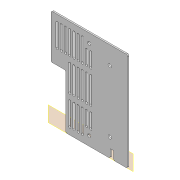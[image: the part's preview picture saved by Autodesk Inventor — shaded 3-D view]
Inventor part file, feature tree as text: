
AUTODESK INVENTOR PART (.ipt)
format: ipt  version: 2020 (Build 240168000, 168)  size: 770,048 bytes
history: native  units: mm
features: other x9, extrude x8, sketch x8, fillet x3, mirror x1
ambient origin geometry x8: Origin, YZ Plane, XZ Plane, XY Plane, X Axis, Y Axis, Z Axis, Center Point
bodies: Body1 (feature_tree)
feature tree (29):
  other  "Sólido1"
  other  "Plano de trabalho1"
  extrude  "Extrusão1"  Depth=0.5mm
  fillet  "Arredondamento2"  Radius=1.0mm
  extrude  "Extrusão5"  Depth=0.5mm
  mirror  "Espelhamento1"
  extrude  "Extrusão6"  Depth=4.5mm
  sketch  "Esboço7"  dims[d7=0.5mm d8=4.5mm]
  extrude  "Extrusão7"  Depth=4.5mm
  extrude  "Extrusão8"  Depth=10.0mm
  sketch  "Esboço9"  dims[d11=18.0mm d12=23.0mm]
  extrude  "Extrusão9"  Depth=18.0mm
  extrude  "Extrusão10"  Depth=31.0mm
  fillet  "Arredondamento3"  Radius=32.0mm
  fillet  "Arredondamento4"  Radius=32.0mm
  extrude  "Extrusão11"  Depth=2.0mm
  sketch  "Esboço1"  dims[d0=0.5mm d1=0.5mm d2=1.0mm]
  other  "Referência1"
  other  "Referência2"
  sketch  "Esboço5"  dims[d3=1.0mm d4=0.5mm]
  sketch  "Esboço6"  dims[d5=0.5mm d6=4.5mm]
  sketch  "Esboço8"  dims[d9=10.0mm d10=10.0mm]
  other  "Contorno projetado3"
  sketch  "Esboço10"  dims[d13=23.0mm d14=31.0mm d15=32.0mm d16=32.0mm]
  other  "Contorno projetado4"
  sketch  "Esboço11"  dims[d17=31.0mm d18=26.0mm d19=3.2mm d20=3.2mm d21=70.0mm d23=6.0mm d24=10.0mm d26=10.0mm d28=2.0mm d29=0.0mm d30=3.2mm d31=6.0mm d32=30.0mm d34=6.0mm d35=10.0mm d37=10.0mm d39=3.2mm d40=6.0mm d41=50.0mm d43=6.0mm d44=10.0mm d46=10.0mm d48=20.0mm d50=6.0mm d51=10.0mm d53=10.0mm d65=2.0mm d66=70.0mm d67=2.2mm d68=0.0mm d69=32.0mm d70=26.0mm d71=19.446305mm d72=32.276848mm d73=3.2mm d74=110.0mm d76=6.0mm d77=10.0mm d79=10.0mm d81=2.2mm d82=0.0mm d83=77.0mm d84=21.0mm d85=2.0mm d86=0.0mm d87=2.0mm d88=0.0mm d90=5.0mm d91=19.8mm d92=12.0mm d93=8.0mm d94=2.0mm d95=0.0mm d96=2.0mm d97=0.0mm d98=2.0mm d99=0.5mm d100=70.0mm d101=140.0mm d102=25.380618mm d103=5.0mm d104=5.0mm d105=44.0mm d106=44.0mm d107=2.0mm d108=0.0mm]
  other  "Calorímetro.iam"
  other  "suporte_fechamento:2"
  other  "suporte_fechamento:3"
